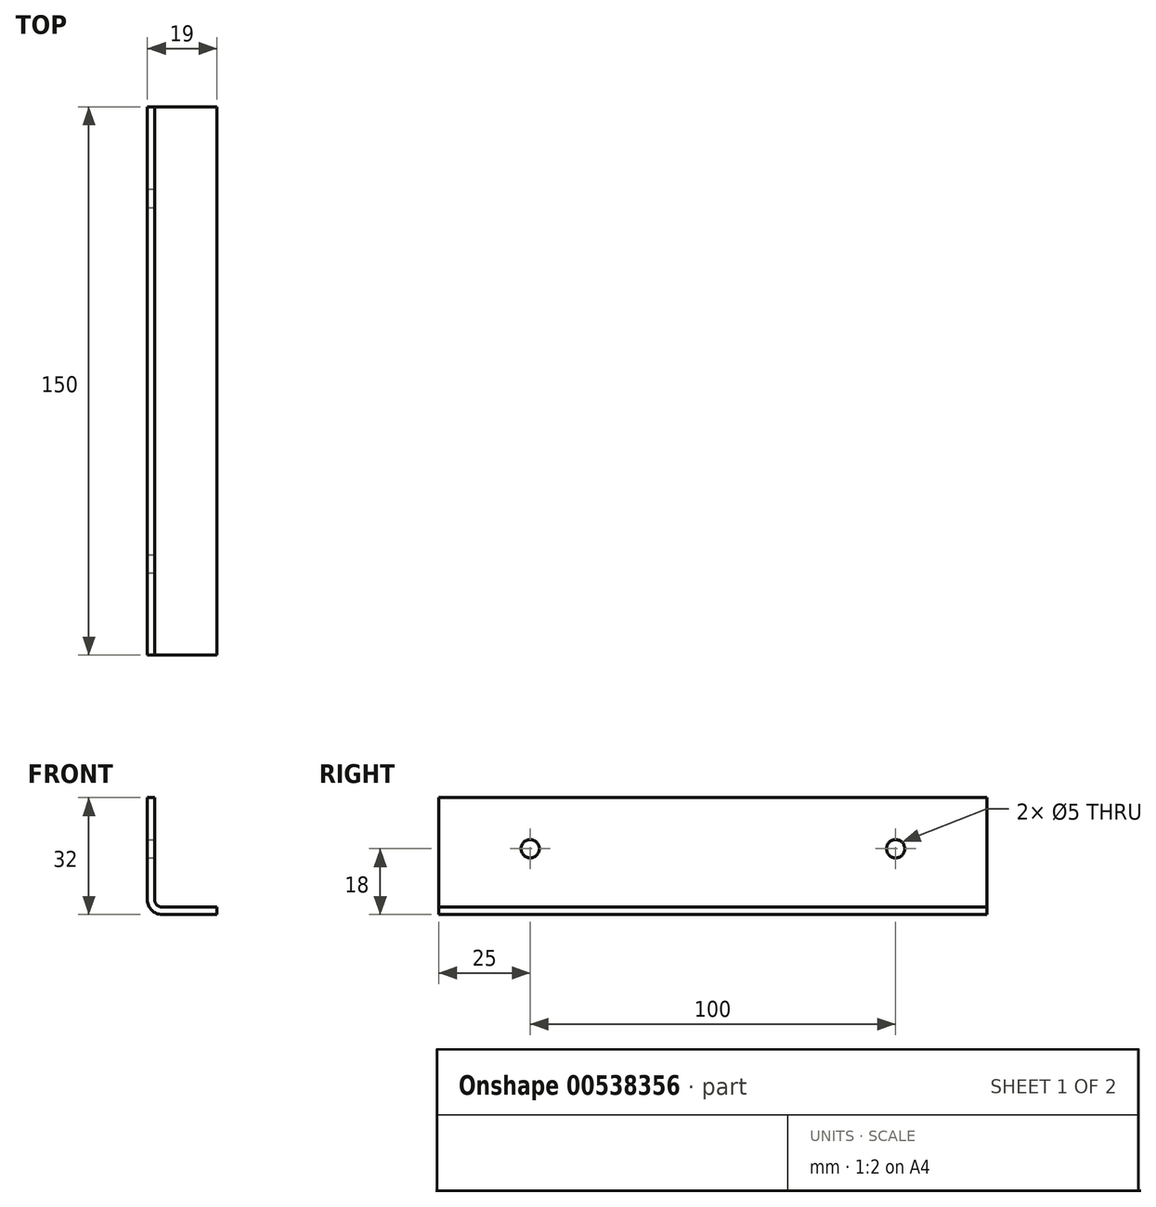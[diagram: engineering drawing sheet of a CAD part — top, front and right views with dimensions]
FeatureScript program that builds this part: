
annotation { "Feature Type Name" : "Feature", "Feature Type Description" : "" }
export const myFeature = defineFeature(function(context is Context, id is Id, definition is map)
    precondition{}
    {
        {
            var Q0;
            Q0=qCreatedBy(makeId("Front.planeOp"),FACE);
            var sketch = newSketch(context, id + "F0", { "sketchPlane" : qUnion([Q0])});
            skLineSegment(sketch, "E0.bottom", {"start": v(0, 0) * mm, "end": v(2, 0) * mm});
            skLineSegment(sketch, "E0.top", {"start": v(0, 30) * mm, "end": v(2, 30) * mm});
            skLineSegment(sketch, "E0.left", {"start": v(0, 2) * mm, "end": v(0, 30) * mm});
            skLineSegment(sketch, "E0.right", {"start": v(2, 2) * mm, "end": v(2, 30) * mm});
            skLineSegment(sketch, "E1", {"start": v(4, -2) * mm, "end": v(19, -2) * mm});
            skLineSegment(sketch, "E2", {"start": v(19, -2) * mm, "end": v(19, 0) * mm});
            skLineSegment(sketch, "E3", {"start": v(19, 0) * mm, "end": v(4, 0) * mm});
            skPoint(sketch, "E4.newPointB", {"position": v(2, 0) * mm});
            skArc(sketch, "E4.filletArc", {"start": v(2, 2) * mm, "mid": v(2.59, 0.59) * mm, "end": v(4, 0) * mm});
            skPoint(sketch, "E5.newPointB", {"position": v(4, -2) * mm});
            skArc(sketch, "E5.filletArc", {"start": v(0, 2) * mm, "mid": v(1.17, -0.83) * mm, "end": v(4, -2) * mm});
            skSolve(sketch);
        }
        {
            var Q0;
            Q0=makeQuery(id+"F0.imprint","IMPRINT",FACE,{"disambiguationData":[TD([[makeQuery(id+"F0.imprint","IMPRINT",EDGE,{"derivedFrom":sQuery(id+"F0.wireOp",EDGE,"E0.top")}),-1.0]])]});
            extrude(context, id + "F1", {"entities" : qUnion([Q0]), "depth" : 150 * mm, "offsetDistance" : 25 * mm});
        }
        {
            var Q0;
            Q0=makeQuery(id+"F1.opExtrude","SWEPT_FACE",FACE,{"disambiguationData":[OSD([sQuery(id+"F0.wireOp",EDGE,"E0.right")])]});
            var sketch = newSketch(context, id + "F2", { "sketchPlane" : qUnion([Q0])});
            skLineSegment(sketch, "E6", {"start": v(-150, 16) * mm, "end": v(0, 16) * mm});
            skLineSegment(sketch, "E7", {"start": v(-125, 30) * mm, "end": v(-125, 4.35) * mm});
            skLineSegment(sketch, "E8", {"start": v(-25, 30) * mm, "end": v(-25, 6.17) * mm});
            skCircle(sketch, "E9", {"center": v(-125, 16) * mm, "radius": 2.5 * mm});
            skCircle(sketch, "E10", {"center": v(-25, 16) * mm, "radius": 2.5 * mm});
            skSolve(sketch);
        }
        {
            var Q0;
            Q0=sQuery(id+"F2.wireOp",VERTEX,"E9.center");
            var Q1;
            Q1=sQuery(id+"F2.wireOp",VERTEX,"E10.center");
            var Q2;
            Q2=makeQuery(id+"F1.opExtrude","SWEPT_BODY",BODY,{"disambiguationData":[OSD([sQuery(id+"F0.wireOp",EDGE,"E0.top"),sQuery(id+"F0.wireOp",EDGE,"E0.left"),sQuery(id+"F0.wireOp",EDGE,"E0.right"),sQuery(id+"F0.wireOp",EDGE,"E1"),sQuery(id+"F0.wireOp",EDGE,"E2"),sQuery(id+"F0.wireOp",EDGE,"E3"),sQuery(id+"F0.wireOp",EDGE,"E4.filletArc"),sQuery(id+"F0.wireOp",EDGE,"E5.filletArc")])]});
            hole(context, id + "F3", {"style" : HoleStyle.SIMPLE, "endStyle" : HoleEndStyle.THROUGH, "holeDiameter" : 5 * mm, "isTappedThrough" : true, "tappedDepth" : 12 * mm, "tapClearance" : 3, "locations" : qUnion([Q0, Q1]), "scope" : qUnion([Q2])});
        }
    });
